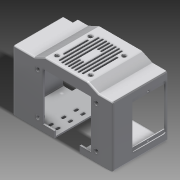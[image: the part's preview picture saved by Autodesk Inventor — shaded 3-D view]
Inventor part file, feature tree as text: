
AUTODESK INVENTOR PART (.ipt)
format: ipt  version: 2015 (Build 190159000, 159)  size: 792,064 bytes
history: native  units: in
note: dims shown in document units (in); Inventor stores cm internally (conversion verified against a paired STEP export)
features: extrude x14, sketch x11, fillet x8, chamfer x5, projected_geometry x4, other x2, plane x1
ambient origin geometry x8: Origin, YZ Plane, XZ Plane, XY Plane, X Axis, Y Axis, Z Axis, Center Point
bodies: Body1 (feature_tree)
feature tree (45):
  plane  "Work Plane1"
  extrude  "Extrusion3"  Depth=0.1181in TaperAngle=0.0deg
  extrude  "Extrusion4"  Depth=0.0787in
  extrude  "Extrusion9"  Depth=0.0787in
  fillet  "Fillet16"  Radius=0.0787in
  chamfer  "Chamfer1"  Distance=0.0394in
  chamfer  "Chamfer2"  Distance=0.2362in
  chamfer  "Chamfer5"  Distance=0.0787in
  fillet  "Fillet5"  Radius=1.5748in
  fillet  "Fillet6"  Radius=2.1654in
  fillet  "Fillet14"  Radius=0.1181in
  extrude  "Extrusion7"  Depth=0.5118in
  other  "Lip1"
  extrude  "Extrusion15"  Depth=1.9685in
  extrude  "Extrusion8"  Depth=0.1181in
  chamfer  "Chamfer4"  Distance=0.0787in
  fillet  "Fillet11"  Radius=0.2362in
  fillet  "Fillet12"  Radius=0.0787in
  extrude  "Extrusion10"  Depth=0.0394in
  extrude  "Extrusion11"  Depth=0.0787in
  extrude  "Extrusion12"  Depth=1.9685in
  fillet  "Fillet13"  Radius=1.9685in
  chamfer  "Chamfer6"  Distance=0.3937in
  extrude  "Extrusion13"  Depth=1.189in
  fillet  "Fillet15"  Radius=0.3937in
  extrude  "Extrusion14"  Depth=0.0394in
  extrude  "Extrusion16"  Depth=0.1969in
  extrude  "Extrusion17"  Depth=0.7874in
  extrude  "Extrusion18"  Depth=1.5748in
  other  "Lip2"
  sketch  "Sketch4"  dims[d10=0.0787in d11=0.0in d12=0.1181in d13=2.4803in d14=0.0in]
  projected_geometry  "Projected Loop2"
  sketch  "Sketch7"  dims[d31=0.0787in d32=0.1575in d33=0.1374in d34=0.0787in d35=0.1575in d36=0.1374in]
  sketch  "Sketch9"  dims[d40=0.0787in d41=0.0787in d46=0.0787in d47=0.0394in d48=0.0in]
  projected_geometry  "Projected Loop3"
  projected_geometry  "Projected Loop4"
  sketch  "Sketch10"  dims[d49=0.0394in d50=0.0394in d51=0.0in d52=0.0in d53=0.0in d54=0.0in]
  sketch  "Sketch11"  dims[d55=0.1181in]
  sketch  "Sketch14"  dims[d58=0.1181in d59=0.2362in d60=0.0in d61=0.0472in d62=0.0787in d63=0.1374in d65=1.5748in d66=2.1654in d70=0.1181in]
  sketch  "Sketch15"  dims[d71=1.0651in d72=0.5118in]
  sketch  "Sketch16"  dims[d73=1.9685in d74=1.0651in]
  sketch  "Sketch17"  dims[d75=0.5118in d76=0.1181in]
  sketch  "Sketch18"  dims[d77=0.0787in]
  sketch  "Sketch19"  dims[d78=0.0787in d79=0.0787in d80=0.2362in d81=0.0in d82=0.0787in d83=0.1575in d84=0.1374in d85=0.0394in d86=0.0787in d87=1.9685in d88=1.9685in d101=0.3937in d102=0.0in d104=1.189in d106=0.3937in d107=0.0in d108=0.1378in d109=0.1969in d110=0.7874in d112=1.5748in d113=0.3937in d115=0.3937in d117=1.5748in d118=1.5855in d119=0.3543in d121=1.1811in d123=0.0787in d124=0.0394in d125=0.0984in d131=0.0787in d132=1.8898in d133=0.0787in d134=0.0394in d135=0.0787in d136=1.9685in d137=0.0787in d138=0.0394in d147=0.0787in d148=0.5906in d151=0.0394in d152=0.0787in d153=1.9685in d154=0.0787in d155=0.0394in d156=0.0787in d157=0.0394in d158=0.7874in d160=1.378in d161=0.3937in d163=0.3937in d165=0.7874in d167=0.6102in d168=0.3937in d170=0.3937in d172=0.374in d175=1.0827in d180=0.0787in d181=0.7874in d183=1.3976in d184=0.3937in d186=0.3937in d188=0.0787in d189=0.315in d190=0.0in d191=0.1969in d193=0.0394in d194=0.0787in d195=45.0deg d196=0.5512in d197=1.0323in d198=0.315in d199=1.4327in d200=2.2579in d201=2.2579in d204=0.0787in d205=0.0787in d206=0.0787in d216=0.0787in d220=0.3543in d221=0.3543in d222=0.3543in d223=0.315in d224=0.1575in d225=0.0787in d226=0.0in d227=0.0394in d228=0.1181in d229=0.1969in d230=0.3937in d231=2.0472in d232=0.0394in d233=0.3937in d234=0.1969in d235=0.1181in d236=2.0472in d237=0.0394in d238=0.1969in d239=0.0in d240=0.0787in d241=0.3543in d243=0.1575in d244=0.1575in d245=0.3937in d246=0.0in d247=0.0787in d248=0.0787in d249=4.7228in d250=4.5654in d259=0.15in d260=0.2362in d261=0.2362in d262=0.15in d263=1.5602in d264=1.2465in d265=2.846in d266=1.7362in d267=1.1811in d269=0.5906in d270=0.3937in d272=0.3937in d274=0.7874in d276=0.315in d277=0.3937in d279=0.3937in d281=0.7874in d283=0.315in d284=0.3937in d286=0.3937in d288=0.1181in d289=0.1181in d290=1.063in d291=0.105in d292=0.105in d293=90.0deg d294=0.7874in d295=0.0in d296=0.5109in d297=0.0394in d298=0.0394in d299=0.0394in d300=0.2362in d301=0.0in d311=0.0787in d313=0.315in d314=0.315in d315=0.315in d316=0.315in d317=0.1181in d318=0.0in d319=0.0394in d320=0.0394in d321=0.0in d322=0.0in d323=0.0in d324=0.0in]
  projected_geometry  "Projected Loop10"
